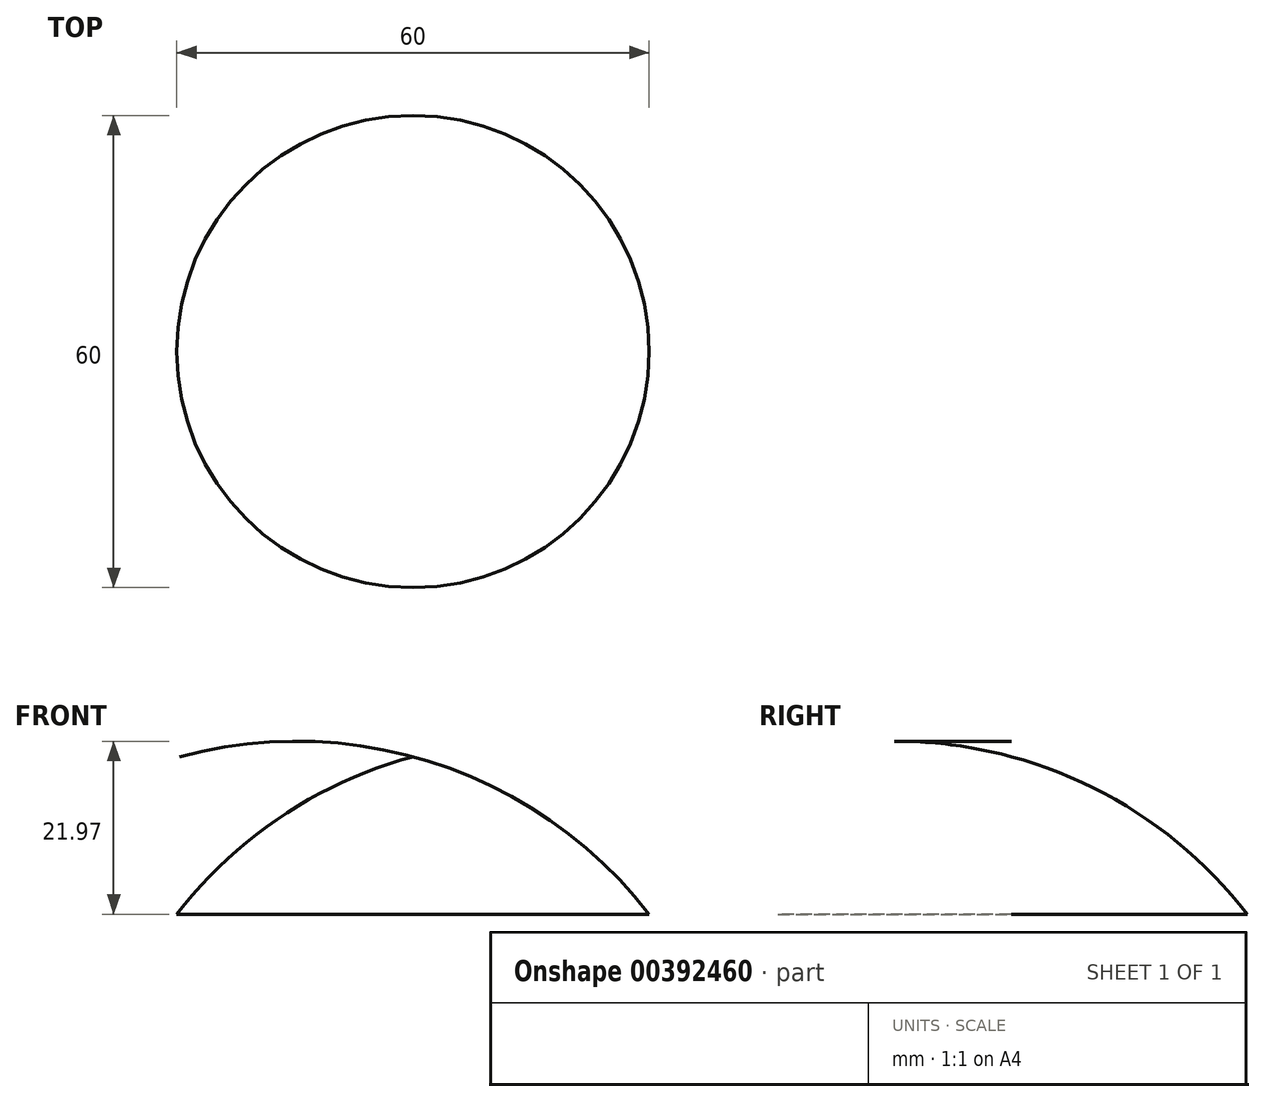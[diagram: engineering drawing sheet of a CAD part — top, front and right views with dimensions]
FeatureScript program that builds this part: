
annotation { "Feature Type Name" : "Feature", "Feature Type Description" : "" }
export const myFeature = defineFeature(function(context is Context, id is Id, definition is map)
    precondition{}
    {
        {
            var Q0;
            Q0=qCreatedBy(makeId("Front.planeOp"),FACE);
            var sketch = newSketch(context, id + "F0", { "sketchPlane" : qUnion([Q0])});
            skLineSegment(sketch, "E0", {"start": v(0, 0) * mm, "end": v(0, 20) * mm});
            skLineSegment(sketch, "E1", {"start": v(0, 0) * mm, "end": v(30, 0) * mm});
            skArc(sketch, "E2", {"start": v(30, 0) * mm, "mid": v(16.63, 12.45) * mm, "end": v(0, 20) * mm});
            skSolve(sketch);
        }
        {
            var Q0;
            Q0=makeQuery(id+"F0.imprint","IMPRINT",FACE,{"disambiguationData":[TD([[makeQuery(id+"F0.imprint","IMPRINT",EDGE,{"derivedFrom":sQuery(id+"F0.wireOp",EDGE,"E0")}),-1.0]])]});
            var Q1;
            Q1=sQuery(id+"F0.wireOp",EDGE,"E0");
            revolve(context, id + "F1", {"entities" : qUnion([Q0]), "axis" : qUnion([Q1]), "revolveType" : RevolveType.FULL});
        }
    });
